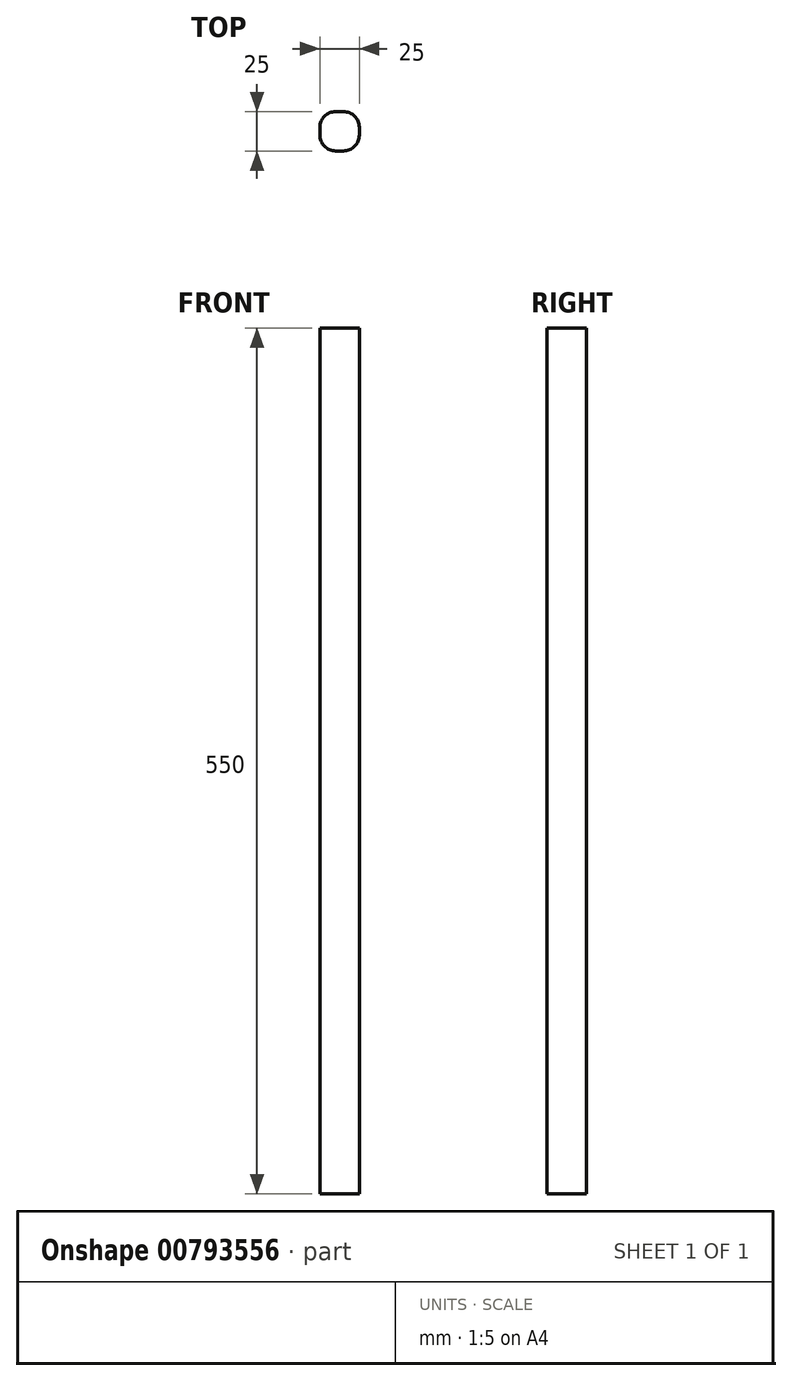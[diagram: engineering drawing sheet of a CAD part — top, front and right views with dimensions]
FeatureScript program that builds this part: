
annotation { "Feature Type Name" : "Feature", "Feature Type Description" : "" }
export const myFeature = defineFeature(function(context is Context, id is Id, definition is map)
    precondition{}
    {
        {
            var Q0;
            Q0=qCreatedBy(makeId("Front.planeOp"),FACE);
            var sketch = newSketch(context, id + "F0", { "sketchPlane" : qUnion([Q0])});
            skLineSegment(sketch, "E0.bottom", {"start": v(0, 0) * mm, "end": v(-25, 0) * mm});
            skLineSegment(sketch, "E0.top", {"start": v(0, 550) * mm, "end": v(-25, 550) * mm});
            skLineSegment(sketch, "E0.left", {"start": v(0, 0) * mm, "end": v(0, 550) * mm});
            skLineSegment(sketch, "E0.right", {"start": v(-25, 0) * mm, "end": v(-25, 550) * mm});
            skSolve(sketch);
        }
        {
            var Q0;
            Q0 = qSketchRegion(id + "F0", true);
            extrude(context, id + "F1", {"entities" : qUnion([Q0]), "depth" : 25 * mm, "offsetDistance" : 25 * mm});
        }
        {
            var Q0;
            Q0=makeQuery(id+"F1.opExtrude","CAP_EDGE",EDGE,{"disambiguationData":[OSD([sQuery(id+"F0.wireOp",EDGE,"E0.right")])],"isStart":false});
            var Q1;
            Q1=makeQuery(id+"F1.opExtrude","CAP_EDGE",EDGE,{"disambiguationData":[OSD([sQuery(id+"F0.wireOp",EDGE,"E0.right")])],"isStart":true});
            var Q2;
            Q2=makeQuery(id+"F1.opExtrude","CAP_EDGE",EDGE,{"disambiguationData":[OSD([sQuery(id+"F0.wireOp",EDGE,"E0.left")])],"isStart":false});
            var Q3;
            Q3=makeQuery(id+"F1.opExtrude","CAP_EDGE",EDGE,{"disambiguationData":[OSD([sQuery(id+"F0.wireOp",EDGE,"E0.left")])],"isStart":true});
            fillet(context, id + "F2", {"entities" : qUnion([Q0, Q1, Q2, Q3]), "radius" : 10 * mm, "tangentPropagation" : true, "allowEdgeOverflow" : false});
        }
    });
